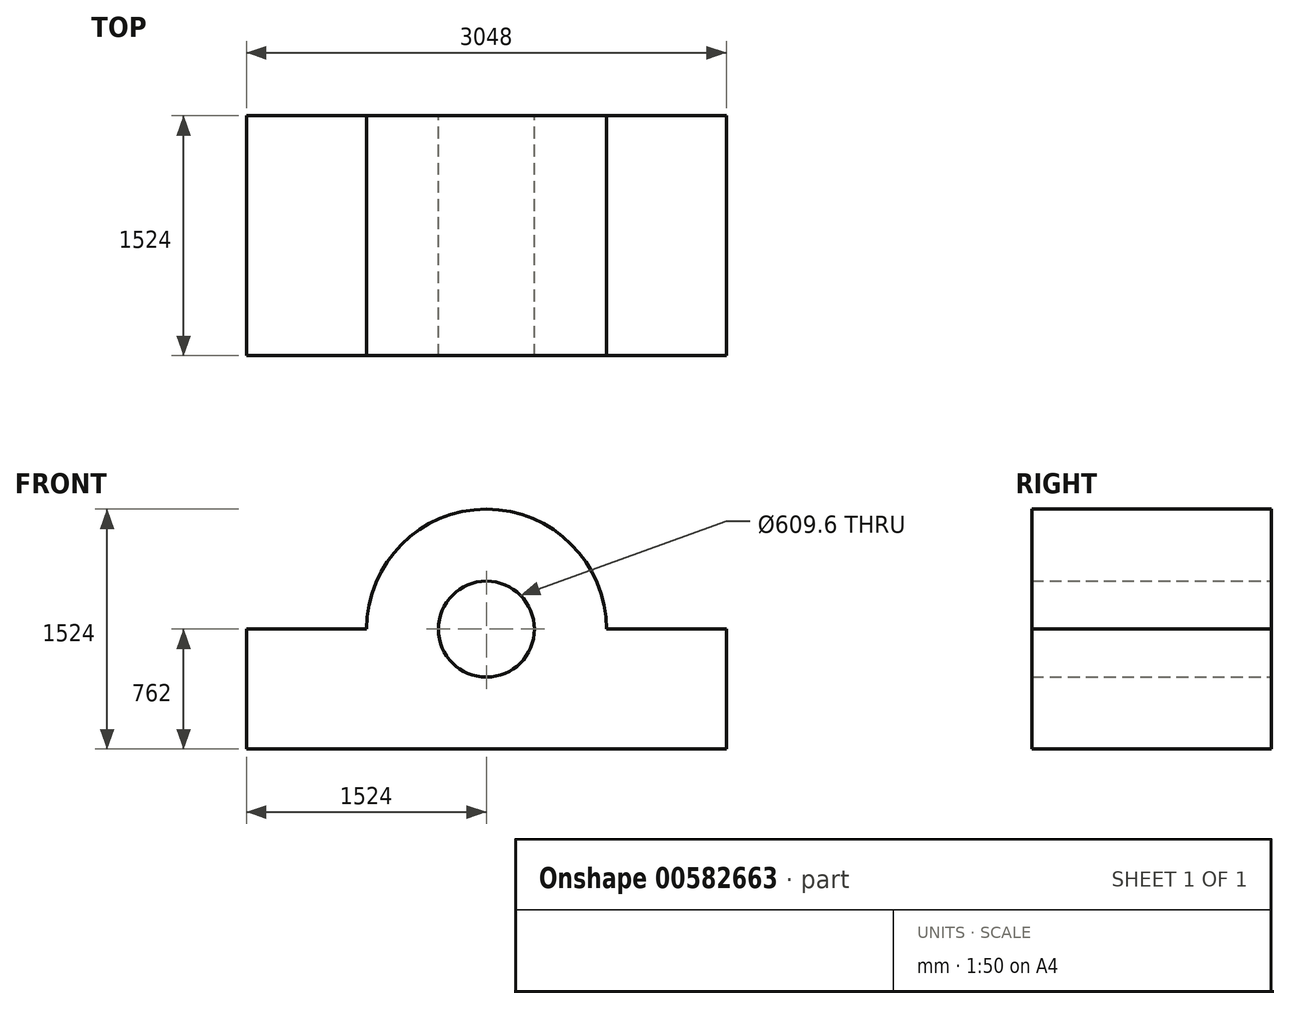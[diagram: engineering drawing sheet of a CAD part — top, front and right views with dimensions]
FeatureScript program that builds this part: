
annotation { "Feature Type Name" : "Feature", "Feature Type Description" : "" }
export const myFeature = defineFeature(function(context is Context, id is Id, definition is map)
    precondition{}
    {
        {
            var Q0;
            Q0=qCreatedBy(makeId("Front.planeOp"),FACE);
            var sketch = newSketch(context, id + "F0", { "sketchPlane" : qUnion([Q0])});
            skLineSegment(sketch, "E0", {"start": v(0, 0) * mm, "end": v(3048, 0) * mm});
            skLineSegment(sketch, "E1", {"start": v(3048, 0) * mm, "end": v(3048, 762) * mm});
            skLineSegment(sketch, "E2", {"start": v(0, 0) * mm, "end": v(0, 762) * mm});
            skLineSegment(sketch, "E3", {"start": v(0, 762) * mm, "end": v(762, 762) * mm});
            skArc(sketch, "E4", {"start": v(2286, 762) * mm, "mid": v(1524, 1524) * mm, "end": v(762, 762) * mm});
            skCircle(sketch, "E5", {"center": v(1524, 762) * mm, "radius": 304.8 * mm});
            skLineSegment(sketch, "E6.trimOffspring", {"start": v(2286, 762) * mm, "end": v(3048, 762) * mm});
            skSolve(sketch);
        }
        {
            var Q0;
            Q0=makeQuery(id+"F0.imprint","IMPRINT",FACE,{"disambiguationData":[TD([[makeQuery(id+"F0.imprint","IMPRINT",EDGE,{"derivedFrom":sQuery(id+"F0.wireOp",EDGE,"E0")}),1.0]])]});
            extrude(context, id + "F1", {"entities" : qUnion([Q0]), "depth" : 1524 * mm, "offsetDistance" : 25.4 * mm});
        }
    });
